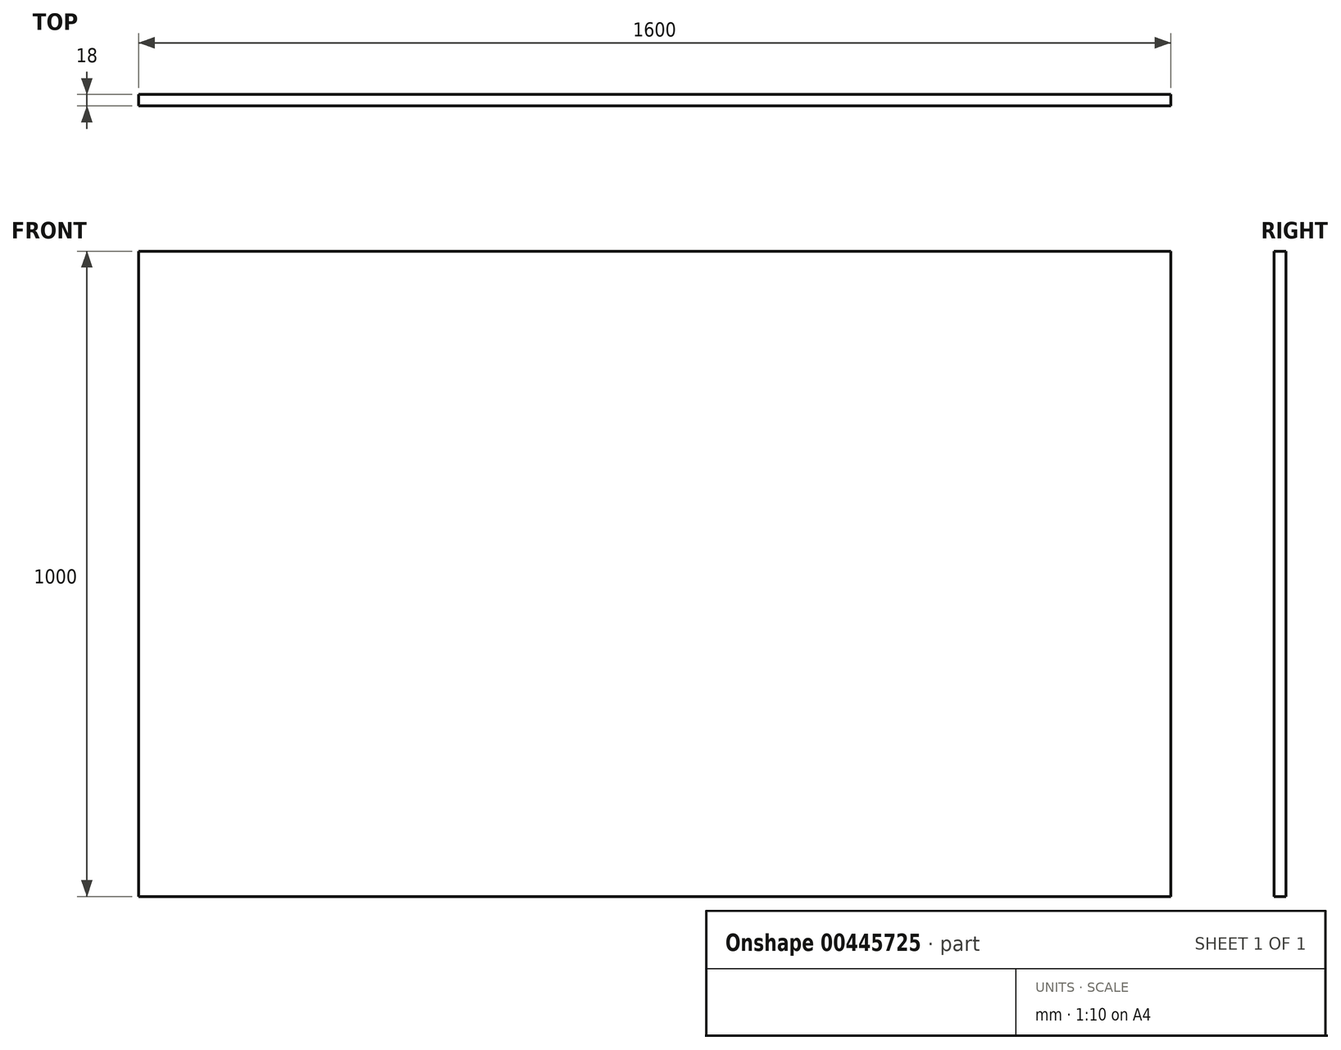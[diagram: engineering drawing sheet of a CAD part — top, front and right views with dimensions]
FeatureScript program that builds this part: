
annotation { "Feature Type Name" : "Feature", "Feature Type Description" : "" }
export const myFeature = defineFeature(function(context is Context, id is Id, definition is map)
    precondition{}
    {
        {
            var Q0;
            Q0=qCreatedBy(makeId("Front.planeOp"),FACE);
            var sketch = newSketch(context, id + "F0", { "sketchPlane" : qUnion([Q0])});
            skLineSegment(sketch, "E0.bottom", {"start": v(0, 0) * mm, "end": v(1600, 0) * mm});
            skLineSegment(sketch, "E0.top", {"start": v(0, -1000) * mm, "end": v(1600, -1000) * mm});
            skLineSegment(sketch, "E0.left", {"start": v(0, 0) * mm, "end": v(0, -1000) * mm});
            skLineSegment(sketch, "E0.right", {"start": v(1600, 0) * mm, "end": v(1600, -1000) * mm});
            skSolve(sketch);
        }
        {
            var Q0;
            Q0 = qSketchRegion(id + "F0", true);
            extrude(context, id + "F1", {"entities" : qUnion([Q0]), "depth" : 18 * mm});
        }
    });
